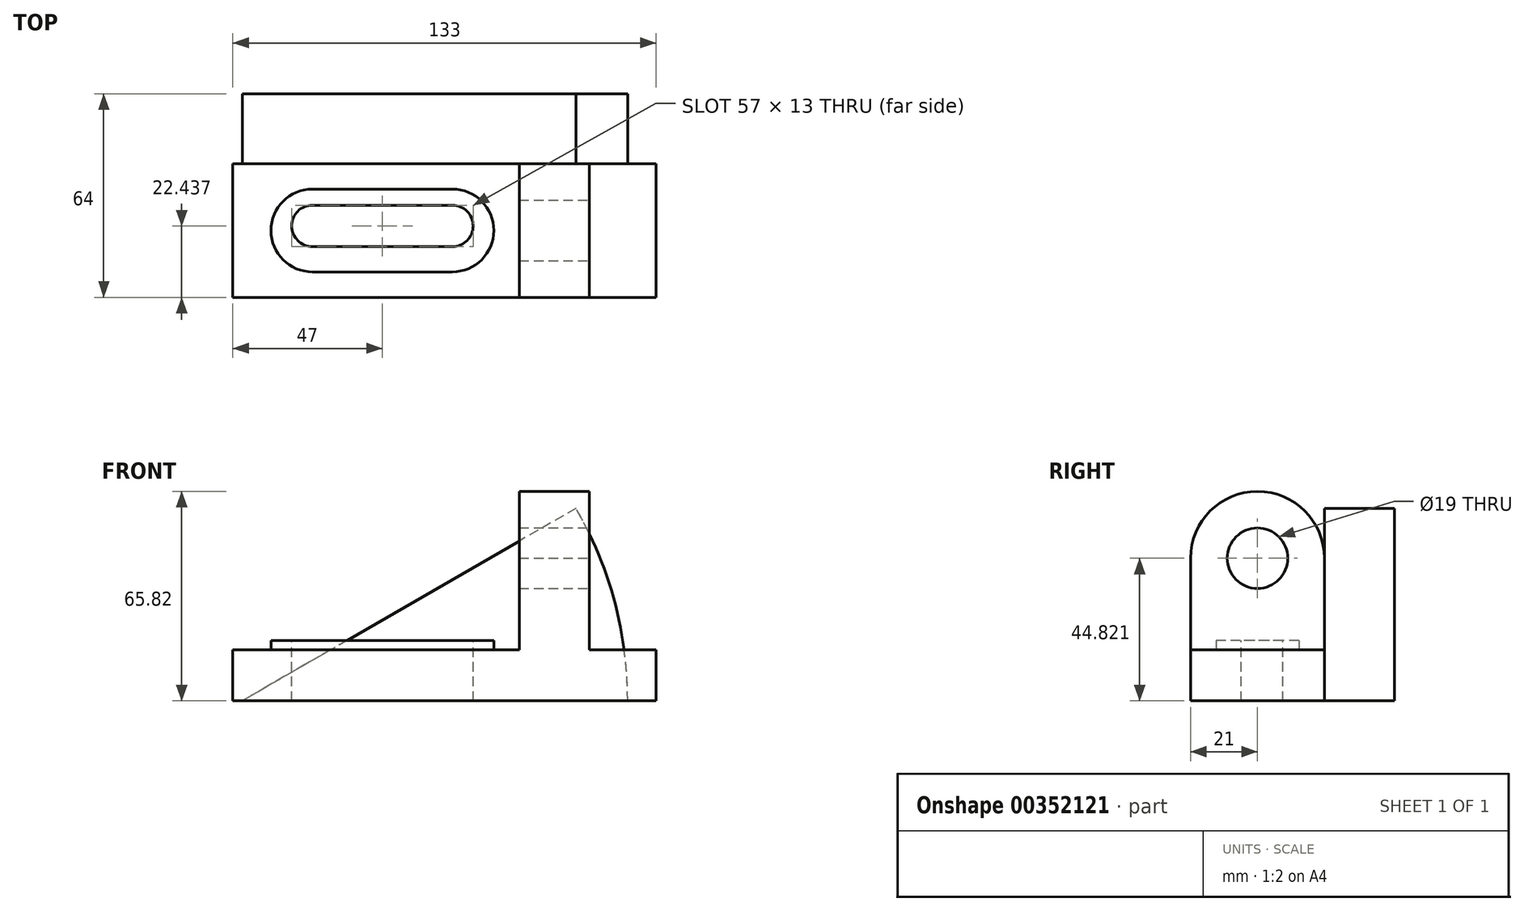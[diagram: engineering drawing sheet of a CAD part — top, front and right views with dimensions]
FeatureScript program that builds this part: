
annotation { "Feature Type Name" : "Feature", "Feature Type Description" : "" }
export const myFeature = defineFeature(function(context is Context, id is Id, definition is map)
    precondition{}
    {
        {
            var Q0;
            Q0=qCreatedBy(makeId("Front.planeOp"),FACE);
            var sketch = newSketch(context, id + "F0", { "sketchPlane" : qUnion([Q0])});
            skLineSegment(sketch, "E0", {"start": v(0, 0) * mm, "end": v(-133, 0) * mm});
            skLineSegment(sketch, "E1", {"start": v(-133, 0) * mm, "end": v(-133, 16) * mm});
            skLineSegment(sketch, "E2", {"start": v(-133, 16) * mm, "end": v(-43, 16) * mm});
            skLineSegment(sketch, "E3", {"start": v(-43, 16) * mm, "end": v(-43, 66) * mm});
            skLineSegment(sketch, "E4", {"start": v(-43, 66) * mm, "end": v(-21, 66) * mm});
            skLineSegment(sketch, "E5", {"start": v(-21, 66) * mm, "end": v(-21, 16) * mm});
            skLineSegment(sketch, "E6", {"start": v(-21, 16) * mm, "end": v(0, 16) * mm});
            skLineSegment(sketch, "E7", {"start": v(0, 16) * mm, "end": v(0, 0) * mm});
            skLineSegment(sketch, "E8", {"start": v(0, 0) * mm, "end": v(0, 0) * mm});
            skSolve(sketch);
        }
        {
            var Q0;
            Q0 = qSketchRegion(id + "F0", true);
            extrude(context, id + "F1", {"entities" : qUnion([Q0]), "depth" : 42 * mm});
        }
        {
            var Q0;
            Q0=makeQuery(id+"F1.opExtrude","SWEPT_FACE",FACE,{"disambiguationData":[OSD([sQuery(id+"F0.wireOp",EDGE,"E5")])]});
            var sketch = newSketch(context, id + "F2", { "sketchPlane" : qUnion([Q0])});
            skLineSegment(sketch, "E9", {"start": v(-42, 44.82) * mm, "end": v(-42, 16) * mm});
            skLineSegment(sketch, "E10", {"start": v(-42, 16) * mm, "end": v(0, 16) * mm});
            skLineSegment(sketch, "E11", {"start": v(0, 16) * mm, "end": v(0, 44.82) * mm});
            skArc(sketch, "E12", {"start": v(0, 44.82) * mm, "mid": v(-21, 65.82) * mm, "end": v(-42, 44.82) * mm});
            skCircle(sketch, "E13", {"center": v(-21, 44.82) * mm, "radius": 9.5 * mm});
            skSolve(sketch);
        }
        {
            var Q0;
            {var subQ0=sQuery(id+"F2.wireOp",EDGE,"E12");Q0=makeQuery(id+"F2.imprint","IMPRINT",FACE,{"disambiguationData":[TD([[makeQuery(id+"F2.imprint","IMPRINT",EDGE,{"derivedFrom":subQ0}),-1.0]])]});}
            extrude(context, id + "F3", {"entities" : qUnion([Q0]), "operationType" : NewBodyOperationType.REMOVE, "endBound" : BoundingType.THROUGH_ALL, "oppositeDirection" : true, "depth" : 25 * mm});
        }
        {
            var Q0;
            Q0=makeQuery(id+"F2.imprint","IMPRINT",FACE,{"disambiguationData":[TD([[makeQuery(id+"F2.imprint","IMPRINT",EDGE,{"derivedFrom":sQuery(id+"F2.wireOp",EDGE,"E13")}),1.0]])]});
            extrude(context, id + "F4", {"entities" : qUnion([Q0]), "operationType" : NewBodyOperationType.REMOVE, "endBound" : BoundingType.THROUGH_ALL, "oppositeDirection" : true, "depth" : 25 * mm});
        }
        {
            var Q0;
            Q0=makeQuery(id+"F1.opExtrude","SWEPT_FACE",FACE,{"disambiguationData":[OSD([sQuery(id+"F0.wireOp",EDGE,"E2")])]});
            var sketch = newSketch(context, id + "F5", { "sketchPlane" : qUnion([Q0])});
            skLineSegment(sketch, "E14", {"start": v(-108, -8) * mm, "end": v(-64, -8) * mm});
            skLineSegment(sketch, "E15", {"start": v(-108, -34) * mm, "end": v(-64, -34) * mm});
            skArc(sketch, "E16", {"start": v(-108, -8) * mm, "mid": v(-121, -21) * mm, "end": v(-108, -34) * mm});
            skArc(sketch, "E17", {"start": v(-64, -34) * mm, "mid": v(-51, -21) * mm, "end": v(-64, -8) * mm});
            skSolve(sketch);
        }
        {
            var Q0;
            Q0 = qSketchRegion(id + "F5", true);
            extrude(context, id + "F6", {"entities" : qUnion([Q0]), "operationType" : NewBodyOperationType.ADD, "depth" : 3 * mm});
        }
        {
            var Q0;
            Q0=qCreatedBy(makeId("Front.planeOp"),FACE);
            var sketch = newSketch(context, id + "F7", { "sketchPlane" : qUnion([Q0])});
            skLineSegment(sketch, "E18", {"start": v(-9, 0) * mm, "end": v(-130, 0) * mm});
            skArc(sketch, "E19", {"start": v(-25.21, 60.5) * mm, "mid": v(-13.12, 31.32) * mm, "end": v(-9, 0) * mm});
            skLineSegment(sketch, "E20", {"start": v(-25.21, 60.5) * mm, "end": v(-130, 0) * mm});
            skSolve(sketch);
        }
        {
            var Q0;
            Q0 = qSketchRegion(id + "F7", true);
            extrude(context, id + "F8", {"entities" : qUnion([Q0]), "operationType" : NewBodyOperationType.ADD, "oppositeDirection" : true, "depth" : 22 * mm});
        }
        {
            var Q0;
            Q0=makeQuery(id+"F6.opExtrude","CAP_FACE",FACE,{"disambiguationData":[OSD([sQuery(id+"F5.wireOp",EDGE,"E14"),sQuery(id+"F5.wireOp",EDGE,"E15"),sQuery(id+"F5.wireOp",EDGE,"E16"),sQuery(id+"F5.wireOp",EDGE,"E17")])],"isStart":false});
            var sketch = newSketch(context, id + "F9", { "sketchPlane" : qUnion([Q0])});
            skLineSegment(sketch, "E21", {"start": v(-108, -13.06) * mm, "end": v(-64, -13.06) * mm});
            skLineSegment(sketch, "E22", {"start": v(-108, -26.06) * mm, "end": v(-64, -26.06) * mm});
            skArc(sketch, "E23", {"start": v(-108, -13.06) * mm, "mid": v(-114.5, -19.56) * mm, "end": v(-108, -26.06) * mm});
            skArc(sketch, "E24", {"start": v(-64, -26.06) * mm, "mid": v(-57.5, -19.56) * mm, "end": v(-64, -13.06) * mm});
            skLineSegment(sketch, "E25", {"start": v(-114.5, -19.56) * mm, "end": v(-57.5, -19.56) * mm, "construction": true});
            skSolve(sketch);
        }
        {
            var Q0;
            Q0=makeQuery(id+"F9.imprint","IMPRINT",FACE,{"disambiguationData":[TD([[makeQuery(id+"F9.imprint","IMPRINT",EDGE,{"derivedFrom":sQuery(id+"F9.wireOp",EDGE,"E21")}),-1.0]])]});
            extrude(context, id + "F10", {"entities" : qUnion([Q0]), "operationType" : NewBodyOperationType.REMOVE, "endBound" : BoundingType.THROUGH_ALL, "oppositeDirection" : true, "depth" : 25 * mm});
        }
    });
